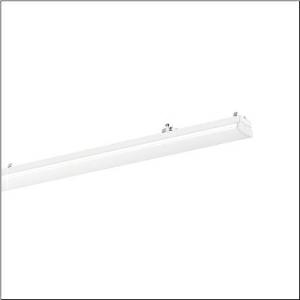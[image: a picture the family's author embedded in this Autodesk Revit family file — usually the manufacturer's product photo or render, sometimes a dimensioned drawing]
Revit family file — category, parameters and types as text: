
# Revit family: licross_r__21_recessed_opal_mo_52tl1dmn36xg_ba94
name_source: partatom
category: Lighting Fixtures
units: mm (PartAtom-declared; Revit-internal decimal feet)

## family parameters
Cut with Voids When Loaded = No
Host = Face
Light Source = No
Part Type = Normal
Room Calculation Point = No
Round Connector Dimension = Use Diameter
Shared = No

## types (1)
- --- (1 x LED, 6300 lm, 37.5 W, 3000K)
    Apparent Load = 38 VA
    CIE Flux Codes = 44 73 91 87 100
    Color Rendering = 80
    Color Temperature = 3000K
    Default Elevation = 1800 mm
    Description = Licross® 21 recessed opal MO, luminaire insert, of sheet steel, galvanised, coil coated, white, length: 1.500mm, width: 66mm, height: 67mm, LED rated luminous flux: 6.300lm, light colour: 830, control gear: ON/OFF Multilumen, with plug, 3-pole, with phase selection, mains connection: 220..240V, AC, 50/60Hz, rated input power: 37.5W, halogen-free wiring, primary optical cover: cover, of PMMA, light emission: direct with ceiling illumination distribution, primary light characteristic: symmetric, protection rating (complete): IP40, insulation class (complete): insulation class I (protective earthing), certification: CE, ENEC, VDE, UKCA, protection symbol: D if used in an environment without relevant dust loads with corresponding accessories, impact resistance: IK06, permissible ambient temperature for indoor applications: -35..+50°C, corresponds to IFS (International Featured Standards) requirements for safety and quality in the food industry, reducing of maximum allowable ambient temperature of 5°C with ceiling mounting, LABS conformity tested according to VDMA 24364:2018-05, packaging unit: 1 piece
    Height = 83 mm
    Lamp = 1 x LED
    Lamp Light Flux = 6300 lm
    Lamp Power = 37.5 W
    Lamp count = 1
    Length = 1500 mm
    Luminous efficacy = 168 lm/W
    Manufacturer = Siteco
    ModVariant = No
    Model = 52TL1DMN36XG
    Mounting Place = Ceiling
    Mounting Type = Pendant
    Number of Poles = 1
    OnlyDefault = Yes
    Power Factor = 1
    Product Name = Licross® 21 recessed opal MO
    Product group = luminaire insert
    ProductGroupID = 902
    Protection Class = Protection class I
    Protection Degree = IP 40
    RLX_Detail_Level = 1
    RLX_Emergency_Light_Flux = 0 lm
    RLX_Emergency_Type = 0
    RLX_Emergency_Type_DB = No
    RlxData = <blob elided: 24705 chars, md5=da859036>
    Socket = socket
    Standby Power = 0 W
    System Light Flux = 6300 lm
    System Power = 38 W
    Type Comments = factory setting: luminous flux: 100 % | (A | C | E) | 87 mA
    Type Image = l_1313666.jpg
    URL = http://relux.com
    VarID = @adj_010299
    Voltage = 0 V
    Weight = 0.00 kg
    Width = 76 mm

## geometry (parser evidence)
native form markers: Blend x4, Sweep x12
no freeform markers — native parametric forms only
